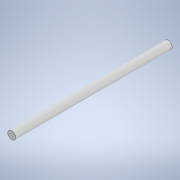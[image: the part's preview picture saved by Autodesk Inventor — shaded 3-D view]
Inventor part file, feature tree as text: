
AUTODESK INVENTOR PART (.ipt)
format: ipt  version: 2020.3 (Build 243373000, 373)  size: 91,136 bytes
history: native  units: mm
features: extrude x1, sketch x1
ambient origin geometry x8: Origin, YZ Plane, XZ Plane, XY Plane, X Axis, Y Axis, Z Axis, Center Point
bodies: Solid1 (feature_tree)
feature tree (2):
  extrude  "Extrusion1"  Depth=160.0mm TaperAngle=0.0deg
  sketch  "Sketch1"  dims[d0=8.0mm d1=160.0mm d2=0.0mm]
